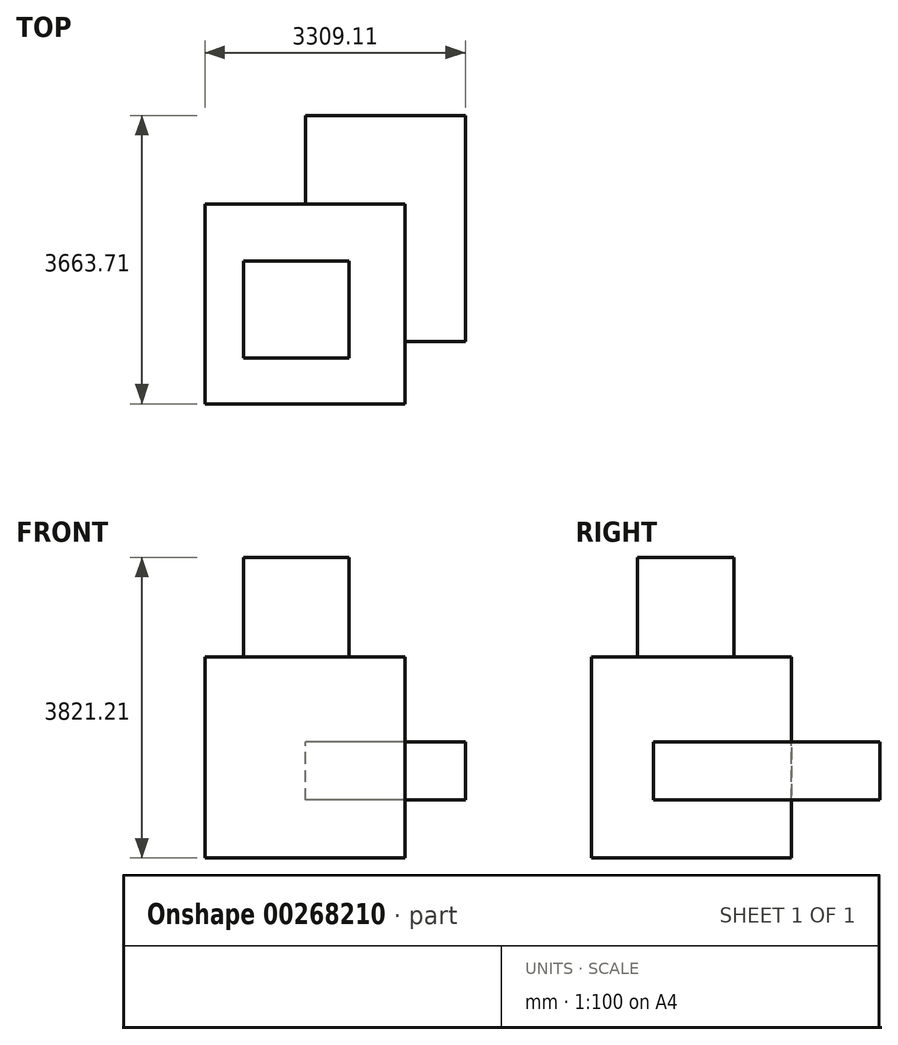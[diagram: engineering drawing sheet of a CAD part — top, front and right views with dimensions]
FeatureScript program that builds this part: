
annotation { "Feature Type Name" : "Feature", "Feature Type Description" : "" }
export const myFeature = defineFeature(function(context is Context, id is Id, definition is map)
    precondition{}
    {
        {
            var Q0;
            Q0=qCreatedBy(makeId("Front.planeOp"),FACE);
            var sketch = newSketch(context, id + "F0", { "sketchPlane" : qUnion([Q0])});
            skLineSegment(sketch, "E0.bottom", {"start": v(-1277.1, 1273.14) * mm, "end": v(1262.9, 1273.14) * mm});
            skLineSegment(sketch, "E0.top", {"start": v(-1277.1, -1281.21) * mm, "end": v(1262.9, -1281.21) * mm});
            skLineSegment(sketch, "E0.left", {"start": v(-1277.1, 1273.14) * mm, "end": v(-1277.1, -1281.21) * mm});
            skLineSegment(sketch, "E0.right", {"start": v(1262.9, 1273.14) * mm, "end": v(1262.9, -1281.21) * mm});
            skSolve(sketch);
        }
        {
            var Q0;
            Q0 = qSketchRegion(id + "F0", true);
            extrude(context, id + "F1", {"entities" : qUnion([Q0]), "depth" : 2540 * mm});
        }
        {
            var Q0;
            Q0=qCreatedBy(makeId("Top.planeOp"),FACE);
            var sketch = newSketch(context, id + "F2", { "sketchPlane" : qUnion([Q0])});
            skLineSegment(sketch, "E1.bottom", {"start": v(-786.78, -726.28) * mm, "end": v(553.7, -726.28) * mm});
            skLineSegment(sketch, "E1.top", {"start": v(-786.78, -1957.34) * mm, "end": v(553.7, -1957.34) * mm});
            skLineSegment(sketch, "E1.left", {"start": v(-786.78, -726.28) * mm, "end": v(-786.78, -1957.34) * mm});
            skLineSegment(sketch, "E1.right", {"start": v(553.7, -726.28) * mm, "end": v(553.7, -1957.34) * mm});
            skSolve(sketch);
        }
        {
            var Q0;
            Q0 = qSketchRegion(id + "F2", true);
            extrude(context, id + "F3", {"entities" : qUnion([Q0]), "operationType" : NewBodyOperationType.ADD, "depth" : 2540 * mm});
        }
        {
            var Q0;
            Q0=qCreatedBy(makeId("Right.planeOp"),FACE);
            var sketch = newSketch(context, id + "F4", { "sketchPlane" : qUnion([Q0])});
            skLineSegment(sketch, "E2.bottom", {"start": v(-1748.74, 194.3) * mm, "end": v(1123.71, 194.3) * mm});
            skLineSegment(sketch, "E2.top", {"start": v(-1748.74, -544.33) * mm, "end": v(1123.71, -544.33) * mm});
            skLineSegment(sketch, "E2.left", {"start": v(-1748.74, 194.3) * mm, "end": v(-1748.74, -544.33) * mm});
            skLineSegment(sketch, "E2.right", {"start": v(1123.71, 194.3) * mm, "end": v(1123.71, -544.33) * mm});
            skSolve(sketch);
        }
        {
            var Q0;
            Q0 = qSketchRegion(id + "F4", true);
            extrude(context, id + "F5", {"entities" : qUnion([Q0]), "operationType" : NewBodyOperationType.ADD, "depth" : 2032 * mm});
        }
    });
